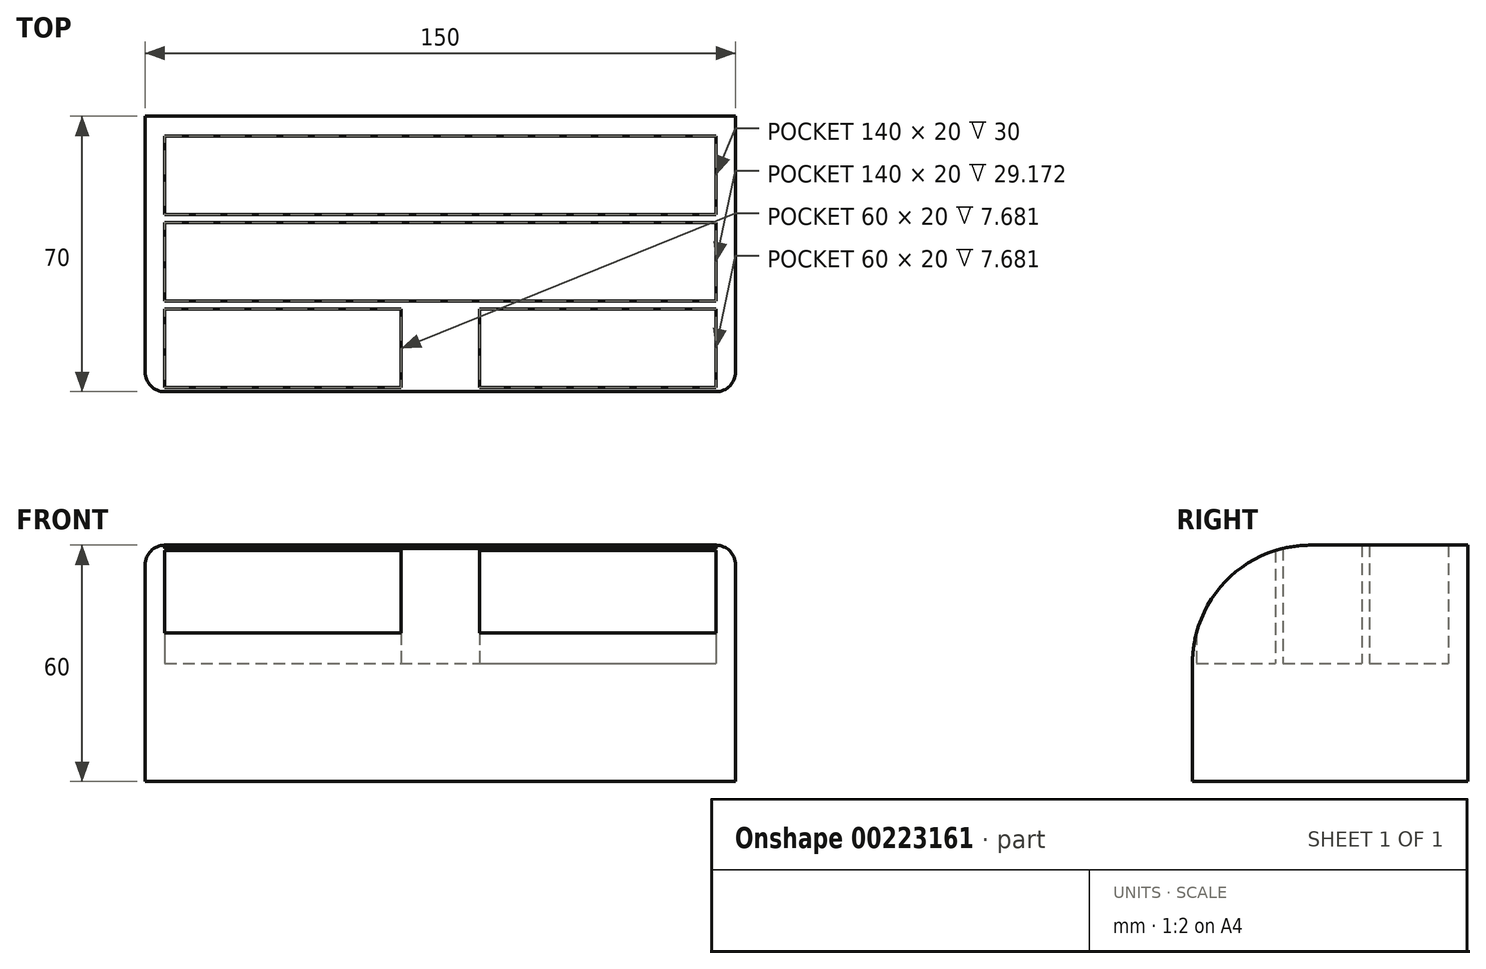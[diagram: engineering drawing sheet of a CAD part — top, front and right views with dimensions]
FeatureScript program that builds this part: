
annotation { "Feature Type Name" : "Feature", "Feature Type Description" : "" }
export const myFeature = defineFeature(function(context is Context, id is Id, definition is map)
    precondition{}
    {
        {
            var Q0;
            Q0=qCreatedBy(makeId("Top.planeOp"),FACE);
            var sketch = newSketch(context, id + "F0", { "sketchPlane" : qUnion([Q0])});
            skLineSegment(sketch, "E0.bottom", {"start": v(75, -35) * mm, "end": v(-75, -35) * mm});
            skLineSegment(sketch, "E0.top", {"start": v(75, 35) * mm, "end": v(-75, 35) * mm});
            skLineSegment(sketch, "E0.left", {"start": v(75, -35) * mm, "end": v(75, 35) * mm});
            skLineSegment(sketch, "E0.right", {"start": v(-75, -35) * mm, "end": v(-75, 35) * mm});
            skPoint(sketch, "E0.middle", {"position": v(0, 0) * mm});
            skLineSegment(sketch, "E1.bottom", {"start": v(70, 10) * mm, "end": v(-70, 10) * mm});
            skLineSegment(sketch, "E1.top", {"start": v(70, 30) * mm, "end": v(-70, 30) * mm});
            skLineSegment(sketch, "E1.left", {"start": v(70, 10) * mm, "end": v(70, 30) * mm});
            skLineSegment(sketch, "E1.right", {"start": v(-70, 10) * mm, "end": v(-70, 30) * mm});
            skPoint(sketch, "E1.middle", {"position": v(0, 20) * mm});
            skLineSegment(sketch, "E2.bottom", {"start": v(70, -12) * mm, "end": v(-70, -12) * mm});
            skLineSegment(sketch, "E2.top", {"start": v(70, 8) * mm, "end": v(-70, 8) * mm});
            skLineSegment(sketch, "E2.left", {"start": v(70, -12) * mm, "end": v(70, 8) * mm});
            skLineSegment(sketch, "E2.right", {"start": v(-70, -12) * mm, "end": v(-70, 8) * mm});
            skPoint(sketch, "E2.middle", {"position": v(0, -2) * mm});
            skPoint(sketch, "E3.middle", {"position": v(0, -24) * mm});
            skLineSegment(sketch, "E4.bottom", {"start": v(10, -14) * mm, "end": v(70, -14) * mm});
            skLineSegment(sketch, "E4.top", {"start": v(10, -34) * mm, "end": v(70, -34) * mm});
            skLineSegment(sketch, "E4.left", {"start": v(10, -14) * mm, "end": v(10, -34) * mm});
            skLineSegment(sketch, "E4.right", {"start": v(70, -14) * mm, "end": v(70, -34) * mm});
            skLineSegment(sketch, "E5.bottom", {"start": v(-70, -14) * mm, "end": v(-10, -14) * mm});
            skLineSegment(sketch, "E5.top", {"start": v(-70, -34) * mm, "end": v(-10, -34) * mm});
            skLineSegment(sketch, "E5.left", {"start": v(-70, -14) * mm, "end": v(-70, -34) * mm});
            skLineSegment(sketch, "E5.right", {"start": v(-10, -14) * mm, "end": v(-10, -34) * mm});
            skSolve(sketch);
        }
        {
            var Q0;
            Q0 = qSketchRegion(id + "F0", true);
            extrude(context, id + "F1", {"entities" : qUnion([Q0]), "depth" : 60 * mm});
        }
        {
            var Q0;
            Q0=makeQuery(id+"F1.opExtrude","CAP_EDGE",EDGE,{"disambiguationData":[OSD([sQuery(id+"F0.wireOp",EDGE,"E0.bottom")])],"isStart":false});
            fillet(context, id + "F2", {"entities" : qUnion([Q0]), "radius" : 30 * mm, "tangentPropagation" : true, "allowEdgeOverflow" : false});
        }
        {
            var Q0;
            Q0=makeQuery(id+"F1.opExtrude","CAP_EDGE",EDGE,{"disambiguationData":[OSD([sQuery(id+"F0.wireOp",EDGE,"E0.left")])],"isStart":false});
            var Q1;
            Q1=makeQuery(id+"F1.opExtrude","CAP_EDGE",EDGE,{"disambiguationData":[OSD([sQuery(id+"F0.wireOp",EDGE,"E0.right")])],"isStart":false});
            fillet(context, id + "F3", {"entities" : qUnion([Q0, Q1]), "radius" : 5 * mm, "tangentPropagation" : true, "allowEdgeOverflow" : false});
        }
        {
            var Q0;
            Q0=makeQuery(id+"F1.opExtrude","CAP_FACE",FACE,{"disambiguationData":[OSD([sQuery(id+"F0.wireOp",EDGE,"E0.bottom"),sQuery(id+"F0.wireOp",EDGE,"E0.top"),sQuery(id+"F0.wireOp",EDGE,"E0.left"),sQuery(id+"F0.wireOp",EDGE,"E0.right"),sQuery(id+"F0.wireOp",EDGE,"E1.bottom"),sQuery(id+"F0.wireOp",EDGE,"E1.top"),sQuery(id+"F0.wireOp",EDGE,"E1.left"),sQuery(id+"F0.wireOp",EDGE,"E1.right")])],"isStart":true});
            var sketch = newSketch(context, id + "F4", { "sketchPlane" : qUnion([Q0])});
            skLineSegment(sketch, "E6.bottom", {"start": v(70, -30) * mm, "end": v(-70, -30) * mm});
            skLineSegment(sketch, "E6.top", {"start": v(70, -9.88) * mm, "end": v(-70, -9.88) * mm});
            skLineSegment(sketch, "E6.left", {"start": v(70, -30) * mm, "end": v(70, -9.88) * mm});
            skLineSegment(sketch, "E6.right", {"start": v(-70, -30) * mm, "end": v(-70, -9.88) * mm});
            skPoint(sketch, "E6.middle", {"position": v(0, -19.94) * mm});
            skLineSegment(sketch, "E7.bottom", {"start": v(70, -8) * mm, "end": v(-70, -8) * mm});
            skLineSegment(sketch, "E7.top", {"start": v(70, 12) * mm, "end": v(-70, 12) * mm});
            skLineSegment(sketch, "E7.left", {"start": v(70, -8) * mm, "end": v(70, 12) * mm});
            skLineSegment(sketch, "E7.right", {"start": v(-70, -8) * mm, "end": v(-70, 12) * mm});
            skPoint(sketch, "E7.middle", {"position": v(0, 2) * mm});
            skLineSegment(sketch, "E8.bottom", {"start": v(70, 14) * mm, "end": v(-70, 14) * mm});
            skLineSegment(sketch, "E8.top", {"start": v(70, 34) * mm, "end": v(-70, 34) * mm});
            skLineSegment(sketch, "E8.left", {"start": v(70, 14) * mm, "end": v(70, 34) * mm});
            skLineSegment(sketch, "E8.right", {"start": v(-70, 14) * mm, "end": v(-70, 34) * mm});
            skPoint(sketch, "E8.middle", {"position": v(0, 24) * mm});
            skSolve(sketch);
        }
        {
            var Q0;
            Q0 = qSketchRegion(id + "F4", true);
            extrude(context, id + "F5", {"entities" : qUnion([Q0]), "operationType" : NewBodyOperationType.ADD, "oppositeDirection" : true, "depth" : 30 * mm});
        }
    });
